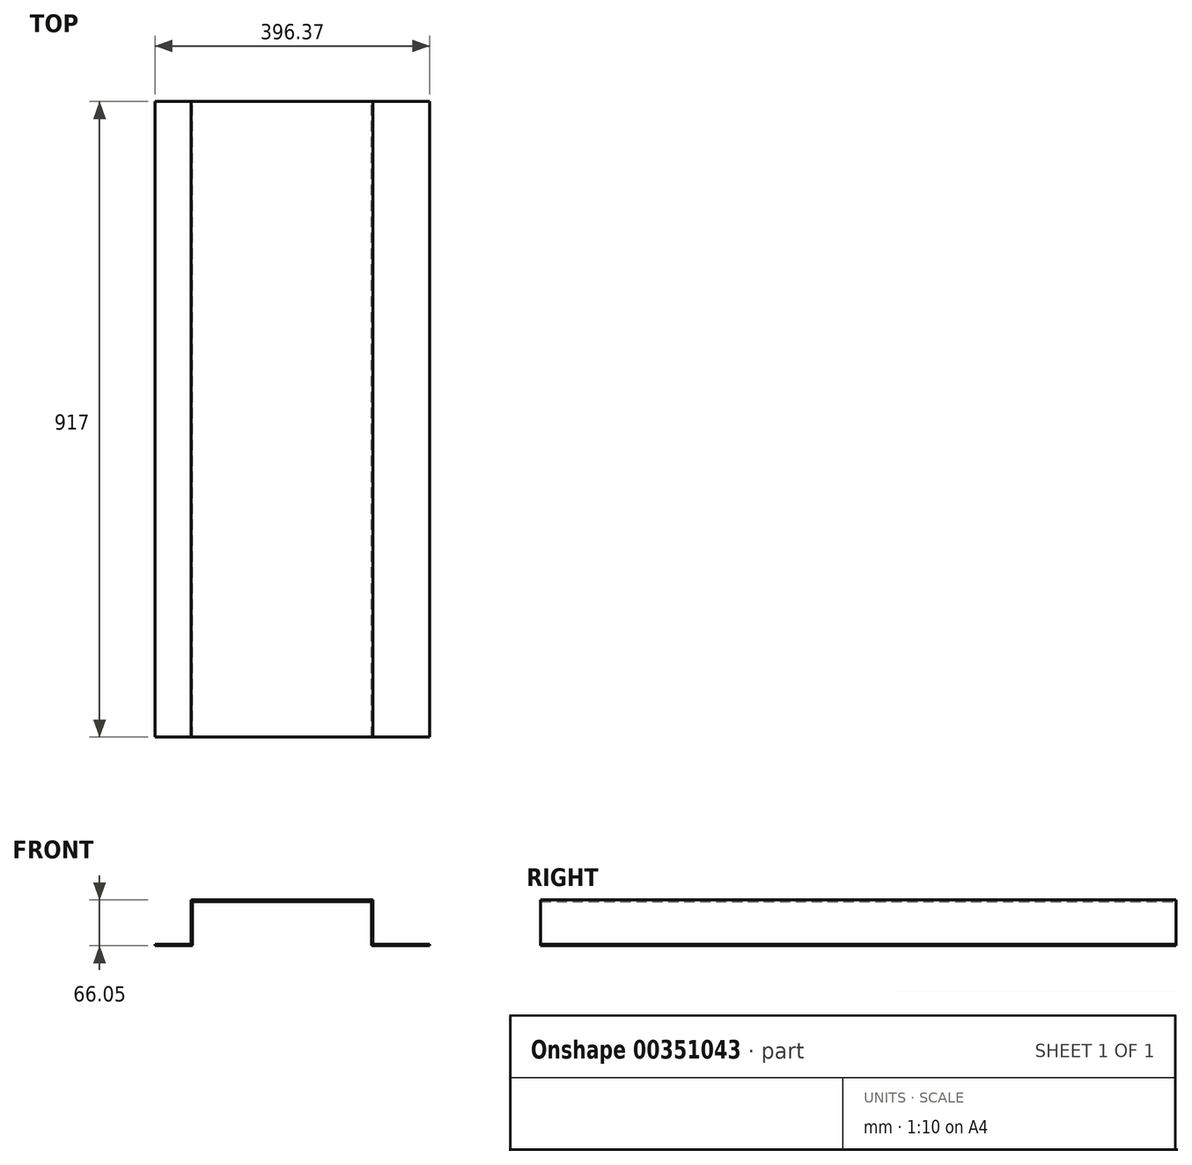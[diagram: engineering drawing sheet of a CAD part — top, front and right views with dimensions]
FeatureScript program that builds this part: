
annotation { "Feature Type Name" : "Feature", "Feature Type Description" : "" }
export const myFeature = defineFeature(function(context is Context, id is Id, definition is map)
    precondition{}
    {
        {
            var Q0;
            Q0=qCreatedBy(makeId("Front.planeOp"),FACE);
            var sketch = newSketch(context, id + "F0", { "sketchPlane" : qUnion([Q0])});
            skLineSegment(sketch, "E0.top", {"start": v(211.5, -66.05) * mm, "end": v(133.36, -66.05) * mm});
            skPoint(sketch, "E0.middle", {"position": v(0, 0) * mm});
            skLineSegment(sketch, "E1.bottom", {"start": v(211.5, -64.05) * mm, "end": v(129.5, -64.05) * mm});
            skLineSegment(sketch, "E2", {"start": v(-132.88, 0) * mm, "end": v(129.5, 0) * mm});
            skLineSegment(sketch, "E3", {"start": v(-184.88, -64.05) * mm, "end": v(-184.88, -66.05) * mm});
            skLineSegment(sketch, "E4", {"start": v(211.5, -64.05) * mm, "end": v(211.5, -66.05) * mm});
            skPoint(sketch, "E0.right.start.orphan", {"position": v(-221, 66.05) * mm});
            skPoint(sketch, "E5.orphan", {"position": v(-221, -66.05) * mm});
            skLineSegment(sketch, "E6", {"start": v(-132.88, 0) * mm, "end": v(-132.88, -64.05) * mm});
            skLineSegment(sketch, "E7", {"start": v(129.5, 0) * mm, "end": v(129.5, -64.05) * mm});
            skLineSegment(sketch, "E8.trimOffspring", {"start": v(-132.88, -64.05) * mm, "end": v(-184.88, -64.05) * mm});
            skLineSegment(sketch, "E9.trimOffspring", {"start": v(-133.36, -66.05) * mm, "end": v(-184.88, -66.05) * mm});
            skLineSegment(sketch, "E10.top", {"start": v(-130.88, -2) * mm, "end": v(127.5, -2) * mm});
            skLineSegment(sketch, "E10.left", {"start": v(-130.88, -66.05) * mm, "end": v(-130.88, -2) * mm});
            skLineSegment(sketch, "E10.right", {"start": v(127.5, -66.05) * mm, "end": v(127.5, -2) * mm});
            skLineSegment(sketch, "E11", {"start": v(-133.36, -66.05) * mm, "end": v(-130.88, -66.05) * mm});
            skLineSegment(sketch, "E12", {"start": v(127.5, -66.05) * mm, "end": v(133.36, -66.05) * mm});
            skSolve(sketch);
        }
        {
            var Q0;
            Q0=qSketchRegion(id+"F0",true);
            extrude(context, id + "F1", {"entities" : qUnion([Q0]), "depth" : 917 * mm});
        }
    });
